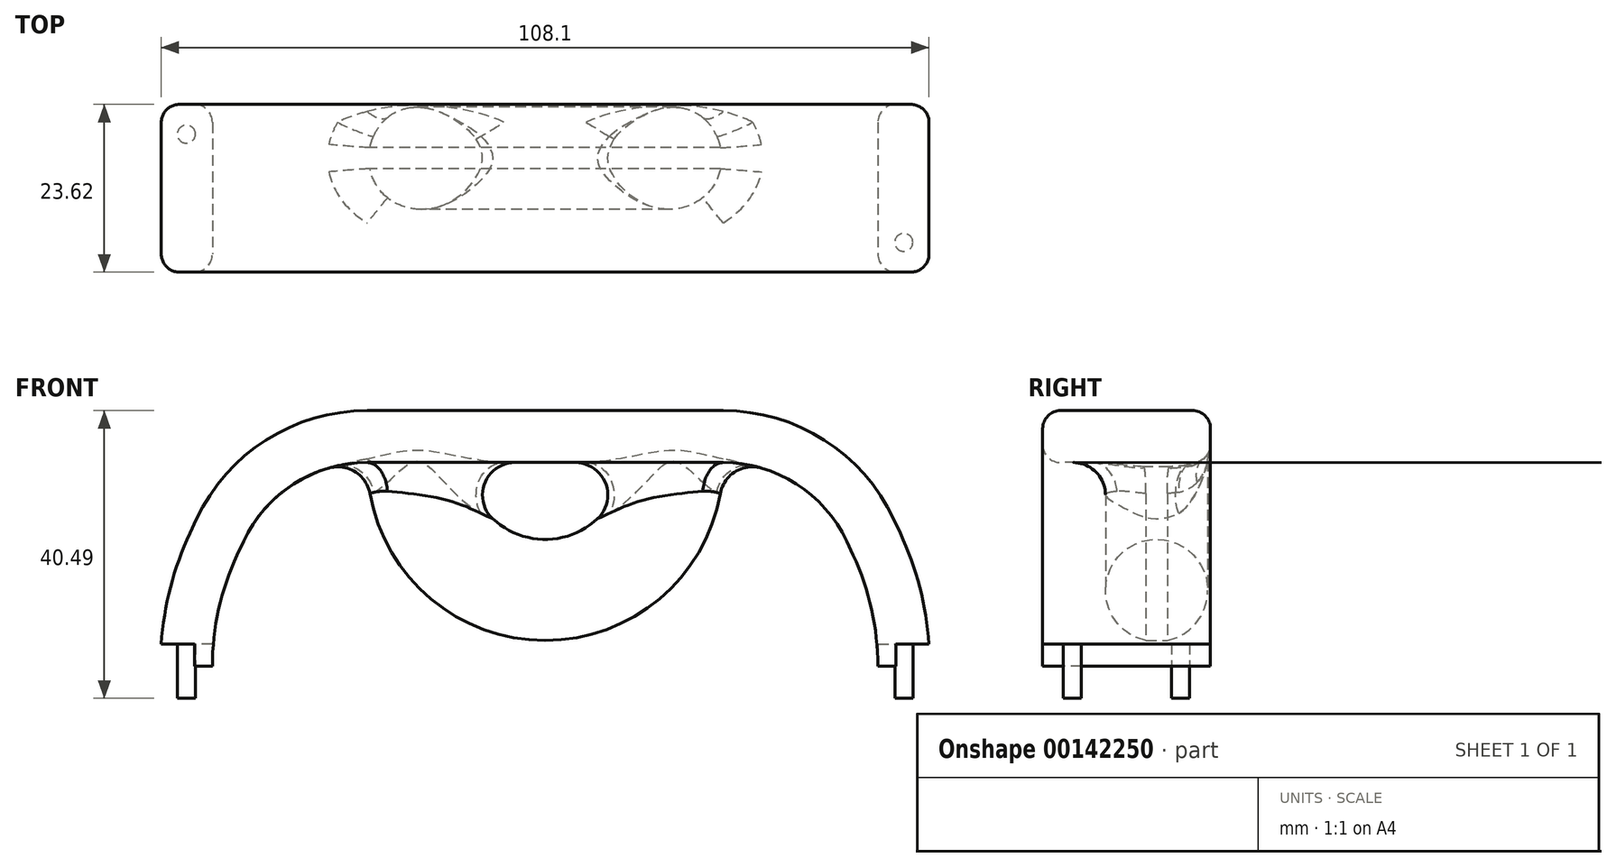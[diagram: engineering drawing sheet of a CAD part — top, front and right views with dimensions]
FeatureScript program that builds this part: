
annotation { "Feature Type Name" : "Feature", "Feature Type Description" : "" }
export const myFeature = defineFeature(function(context is Context, id is Id, definition is map)
    precondition{}
    {
        {
            var Q0;
            Q0=qCreatedBy(makeId("Top.planeOp"),FACE);
            var sketch = newSketch(context, id + "F0", { "sketchPlane" : qUnion([Q0])});
            skLineSegment(sketch, "E0.bottom", {"start": v(49.38, 11.8) * mm, "end": v(51.62, 11.8) * mm});
            skLineSegment(sketch, "E0.top", {"start": v(49.38, -11.8) * mm, "end": v(51.62, -11.8) * mm});
            skLineSegment(sketch, "E0.left", {"start": v(54.16, 9.27) * mm, "end": v(54.16, -9.27) * mm});
            skLineSegment(sketch, "E0.right", {"start": v(46.84, 9.27) * mm, "end": v(46.84, -9.27) * mm});
            skLineSegment(sketch, "E1", {"start": v(0, 14.57) * mm, "end": v(0, -26.63) * mm, "construction": true});
            skCircle(sketch, "E2", {"center": v(50.5, 7.62) * mm, "radius": 1.27 * mm});
            skLineSegment(sketch, "E3", {"start": v(50.5, 11.8) * mm, "end": v(50.5, -11.8) * mm, "construction": true});
            skLineSegment(sketch, "E4", {"start": v(46.84, 0) * mm, "end": v(54.16, 0) * mm, "construction": true});
            skCircle(sketch, "E5.MirrorC", {"center": v(50.5, -7.62) * mm, "radius": 1.27 * mm});
            skLineSegment(sketch, "E6", {"start": v(-32.84, 0) * mm, "end": v(42.72, 0) * mm, "construction": true});
            skCircle(sketch, "E7.MirrorC", {"center": v(-50.5, 7.62) * mm, "radius": 1.27 * mm});
            skCircle(sketch, "E8.MirrorC", {"center": v(-50.5, -7.62) * mm, "radius": 1.27 * mm});
            skPoint(sketch, "E9.visualSharp", {"position": v(46.84, 11.8) * mm});
            skArc(sketch, "E9.filletArc", {"start": v(49.38, 11.8) * mm, "mid": v(47.59, 11.06) * mm, "end": v(46.84, 9.27) * mm});
            skPoint(sketch, "E10.visualSharp", {"position": v(54.16, 11.8) * mm});
            skArc(sketch, "E10.filletArc", {"start": v(54.16, 9.27) * mm, "mid": v(53.41, 11.06) * mm, "end": v(51.62, 11.8) * mm});
            skPoint(sketch, "E11.visualSharp", {"position": v(46.84, -11.8) * mm});
            skArc(sketch, "E11.filletArc", {"start": v(46.84, -9.27) * mm, "mid": v(47.59, -11.06) * mm, "end": v(49.38, -11.8) * mm});
            skPoint(sketch, "E12.visualSharp", {"position": v(54.16, -11.8) * mm});
            skArc(sketch, "E12.filletArc", {"start": v(51.62, -11.8) * mm, "mid": v(53.41, -11.06) * mm, "end": v(54.16, -9.27) * mm});
            skLineSegment(sketch, "E13.MirrorCS", {"start": v(-46.84, 9.27) * mm, "end": v(-46.84, -9.27) * mm});
            skArc(sketch, "E14.MirrorCS", {"start": v(-49.38, 11.8) * mm, "mid": v(-47.59, 11.06) * mm, "end": v(-46.84, 9.27) * mm});
            skLineSegment(sketch, "E15.MirrorCS", {"start": v(-49.38, 11.8) * mm, "end": v(-51.62, 11.8) * mm});
            skArc(sketch, "E16.MirrorCS", {"start": v(-54.16, 9.27) * mm, "mid": v(-53.41, 11.06) * mm, "end": v(-51.62, 11.8) * mm});
            skLineSegment(sketch, "E17.MirrorCS", {"start": v(-54.16, 9.27) * mm, "end": v(-54.16, -9.27) * mm});
            skArc(sketch, "E18.MirrorCS", {"start": v(-51.62, -11.8) * mm, "mid": v(-53.41, -11.06) * mm, "end": v(-54.16, -9.27) * mm});
            skLineSegment(sketch, "E19.MirrorCS", {"start": v(-49.38, -11.8) * mm, "end": v(-51.62, -11.8) * mm});
            skArc(sketch, "E20.MirrorCS", {"start": v(-46.84, -9.27) * mm, "mid": v(-47.59, -11.06) * mm, "end": v(-49.38, -11.8) * mm});
            skSolve(sketch);
        }
        {
            var Q0;
            Q0=qCreatedBy(makeId("Front.planeOp"),FACE);
            var sketch = newSketch(context, id + "F1", { "sketchPlane" : qUnion([Q0])});
            skPoint(sketch, "E21.0", {"position": v(-50.5, 0) * mm});
            skPoint(sketch, "E22.0", {"position": v(50.5, 0) * mm});
            skLineSegment(sketch, "E23", {"start": v(-50.5, 0) * mm, "end": v(-50.5, 4.48) * mm});
            skLineSegment(sketch, "E24", {"start": v(-46.68, 21.68) * mm, "end": v(-45.76, 23.64) * mm});
            skLineSegment(sketch, "E25", {"start": v(-25.05, 36.83) * mm, "end": v(0, 36.83) * mm});
            skLineSegment(sketch, "E26", {"start": v(0, 38.28) * mm, "end": v(0, -45.27) * mm, "construction": true});
            skPoint(sketch, "E27.visualSharp", {"position": v(-39.6, 36.83) * mm});
            skArc(sketch, "E27.filletArc", {"start": v(-25.05, 36.83) * mm, "mid": v(-37.33, 33.25) * mm, "end": v(-45.76, 23.64) * mm});
            skPoint(sketch, "E28.visualSharp", {"position": v(-50.5, 13.5) * mm});
            skArc(sketch, "E28.filletArc", {"start": v(-46.68, 21.68) * mm, "mid": v(-49.53, 13.29) * mm, "end": v(-50.5, 4.48) * mm});
            skLineSegment(sketch, "E29.MirrorCS", {"start": v(25.05, 36.83) * mm, "end": v(0, 36.83) * mm});
            skArc(sketch, "E30.MirrorCS", {"start": v(25.05, 36.83) * mm, "mid": v(37.33, 33.25) * mm, "end": v(45.76, 23.64) * mm});
            skLineSegment(sketch, "E31.MirrorCS", {"start": v(46.68, 21.68) * mm, "end": v(45.76, 23.64) * mm});
            skArc(sketch, "E32.MirrorCS", {"start": v(46.68, 21.68) * mm, "mid": v(49.53, 13.29) * mm, "end": v(50.5, 4.48) * mm});
            skLineSegment(sketch, "E33.MirrorCS", {"start": v(50.5, 0) * mm, "end": v(50.5, 4.48) * mm});
            skSolve(sketch);
        }
        {
            var Q0;
            Q0=makeQuery(id+"F0.imprint","IMPRINT",FACE,{"disambiguationData":[TD([[makeQuery(id+"F0.imprint","IMPRINT",EDGE,{"derivedFrom":sQuery(id+"F0.wireOp",EDGE,"E7.MirrorC")}),1.0]])]});
            var Q1;
            Q1=makeQuery(id+"F0.imprint","IMPRINT",FACE,{"disambiguationData":[TD([[makeQuery(id+"F0.imprint","IMPRINT",EDGE,{"derivedFrom":sQuery(id+"F0.wireOp",EDGE,"E8.MirrorC")}),1.0]])]});
            var Q2;
            Q2=makeQuery(id+"F0.imprint","IMPRINT",FACE,{"disambiguationData":[TD([[makeQuery(id+"F0.imprint","IMPRINT",EDGE,{"derivedFrom":sQuery(id+"F0.wireOp",EDGE,"E7.MirrorC")}),-1.0]])]});
            var Q3;
            Q3=sQuery(id+"F1.wireOp",EDGE,"E23");
            var Q4;
            Q4=sQuery(id+"F1.wireOp",EDGE,"E28.filletArc");
            var Q5;
            Q5=sQuery(id+"F1.wireOp",EDGE,"E24");
            var Q6;
            Q6=sQuery(id+"F1.wireOp",EDGE,"E27.filletArc");
            var Q7;
            Q7=sQuery(id+"F1.wireOp",EDGE,"E25");
            var Q8;
            Q8=sQuery(id+"F1.wireOp",EDGE,"E29.MirrorCS");
            var Q9;
            Q9=sQuery(id+"F1.wireOp",EDGE,"E30.MirrorCS");
            var Q10;
            Q10=sQuery(id+"F1.wireOp",EDGE,"E31.MirrorCS");
            var Q11;
            Q11=sQuery(id+"F1.wireOp",EDGE,"E32.MirrorCS");
            var Q12;
            Q12=sQuery(id+"F1.wireOp",EDGE,"E33.MirrorCS");
            sweep(context, id + "F2", {"profiles" : qUnion([Q0, Q1, Q2]), "path" : qUnion([Q3, Q4, Q5, Q6, Q7, Q8, Q9, Q10, Q11, Q12])});
        }
        {
            var Q0;
            Q0=makeQuery(id+"F2.opSweep","SWEPT_FACE",FACE,{"disambiguationData":[OSD([sQuery(id+"F0.wireOp",EDGE,"E13.MirrorCS"),sQuery(id+"F1.wireOp",EDGE,"E25")])]});
            var sketch = newSketch(context, id + "F3", { "sketchPlane" : qUnion([Q0])});
            skLineSegment(sketch, "E34", {"start": v(0, -17.35) * mm, "end": v(0, 18.28) * mm, "construction": true});
            skPoint(sketch, "E34.endSnap0", {"position": v(0, 9.27) * mm});
            skLineSegment(sketch, "E35.0", {"start": v(-25.05, -11.8) * mm, "end": v(25.05, -11.8) * mm, "construction": true});
            skLineSegment(sketch, "E36.0", {"start": v(-25.05, 11.8) * mm, "end": v(25.05, 11.8) * mm, "construction": true});
            skCircle(sketch, "E37", {"center": v(18.01, -4.23) * mm, "radius": 7.2 * mm});
            skSolve(sketch);
        }
        {
            var Q0;
            {var subQ0=sQuery(id+"F3.wireOp",EDGE,"E37");var subQ1=makeQuery(id+"F2.opSweep","SWEPT_EDGE",EDGE,{"disambiguationData":[OSD([sQuery(id+"F0.wireOp",EDGE,"E13.MirrorCS"),sQuery(id+"F0.wireOp",EDGE,"E14.MirrorCS"),sQuery(id+"F1.wireOp",EDGE,"E25")])]});var subQ2=makeQuery(id+"F3.imprint","INTERSECT",VERTEX,{"disambiguationData":[OD(0.0)],"derivedFrom":[subQ1,subQ0]});Q0=makeQuery(id+"F3.imprint","IMPRINT",FACE,{"disambiguationData":[TD([[makeQuery(id+"F3.imprint","IMPRINT",EDGE,{"disambiguationData":[TD([[subQ2,-1.0]])],"derivedFrom":subQ0}),1.0]])]});}
            var Q1;
            {var subQ0=sQuery(id+"F3.wireOp",EDGE,"E37");var subQ1=makeQuery(id+"F2.opSweep","SWEPT_EDGE",EDGE,{"disambiguationData":[OSD([sQuery(id+"F0.wireOp",EDGE,"E13.MirrorCS"),sQuery(id+"F0.wireOp",EDGE,"E14.MirrorCS"),sQuery(id+"F1.wireOp",EDGE,"E25")])]});var subQ2=makeQuery(id+"F3.imprint","INTERSECT",VERTEX,{"disambiguationData":[OD(0.0)],"derivedFrom":[subQ1,subQ0]});Q1=makeQuery(id+"F3.imprint","IMPRINT",FACE,{"disambiguationData":[TD([[makeQuery(id+"F3.imprint","IMPRINT",EDGE,{"disambiguationData":[TD([[subQ2,1.0]])],"derivedFrom":subQ0}),1.0]])]});}
            var Q2;
            Q2=sQuery(id+"F3.wireOp",EDGE,"E34");
            revolve(context, id + "F4", {"operationType" : NewBodyOperationType.ADD, "entities" : qUnion([Q0, Q1]), "axis" : qUnion([Q2]), "revolveType" : RevolveType.TWO_DIRECTIONS, "angle" : 15.1 * degree, "angleBack" : 164.53 * degree});
        }
        {
            var Q0;
            Q0=makeQuery(id+"F4.boolean.opBoolean","INTERSECT",EDGE,{"disambiguationData":[OD(1.0)],"derivedFrom":[makeQuery(id+"F2.opSweep","SWEPT_FACE",FACE,{"disambiguationData":[OSD([sQuery(id+"F0.wireOp",EDGE,"E13.MirrorCS"),sQuery(id+"F1.wireOp",EDGE,"E25")])]}),makeQuery(id+"F4.opRevolve","SWEPT_FACE",FACE,{"disambiguationData":[OSD([sQuery(id+"F3.wireOp",EDGE,"E37")])]})]});
            var Q1;
            {var subQ0=sQuery(id+"F0.wireOp",EDGE,"E13.MirrorCS");var subQ1=sQuery(id+"F1.wireOp",VERTEX,"E30.MirrorCS.start");Q1=makeQuery(id+"F4.boolean.opBoolean","SPLIT",EDGE,{"disambiguationData":[topologyDisambiguationEdgeConnected([makeQuery(id+"F2.opSweep","SWEPT_FACE",FACE,{"disambiguationData":[OSD([subQ0,sQuery(id+"F1.wireOp",EDGE,"E30.MirrorCS")])]}),makeQuery(id+"F4.opRevolve","SWEPT_FACE",FACE,{"disambiguationData":[OSD([subQ0,subQ1])]})])],"derivedFrom":makeQuery(id+"F2.opSweep","MID_CAP_EDGE",EDGE,{"disambiguationData":[OSD([subQ0,subQ1])],"capPos":6.0})});}
            var Q2;
            Q2=makeQuery(id+"F4.boolean.opBoolean","INTERSECT",EDGE,{"disambiguationData":[OD(0.0)],"derivedFrom":[makeQuery(id+"F2.opSweep","SWEPT_FACE",FACE,{"disambiguationData":[OSD([sQuery(id+"F0.wireOp",EDGE,"E14.MirrorCS"),sQuery(id+"F1.wireOp",EDGE,"E25")])]}),makeQuery(id+"F4.opRevolve","SWEPT_FACE",FACE,{"disambiguationData":[OSD([sQuery(id+"F3.wireOp",EDGE,"E37")])]})]});
            var Q3;
            Q3=makeQuery(id+"F4.boolean.opBoolean","INTERSECT",EDGE,{"disambiguationData":[OD(2.0)],"derivedFrom":[makeQuery(id+"F2.opSweep","SWEPT_FACE",FACE,{"disambiguationData":[OSD([sQuery(id+"F0.wireOp",EDGE,"E13.MirrorCS"),sQuery(id+"F1.wireOp",EDGE,"E25")])]}),makeQuery(id+"F4.opRevolve","SWEPT_FACE",FACE,{"disambiguationData":[OSD([sQuery(id+"F3.wireOp",EDGE,"E37")])]})]});
            var Q4;
            {var subQ0=sQuery(id+"F0.wireOp",EDGE,"E13.MirrorCS");Q4=makeQuery(id+"F4.boolean.opBoolean","SPLIT",EDGE,{"disambiguationData":[topologyDisambiguationEdgeConnected([makeQuery(id+"F2.opSweep","SWEPT_FACE",FACE,{"disambiguationData":[OSD([subQ0,sQuery(id+"F1.wireOp",EDGE,"E27.filletArc")])]}),makeQuery(id+"F4.opRevolve","SWEPT_FACE",FACE,{"disambiguationData":[OSD([subQ0,sQuery(id+"F1.wireOp",VERTEX,"E30.MirrorCS.start")])]})])],"derivedFrom":makeQuery(id+"F2.opSweep","MID_CAP_EDGE",EDGE,{"disambiguationData":[OSD([subQ0,sQuery(id+"F1.wireOp",VERTEX,"E25.start")])],"capPos":4.0})});}
            fillet(context, id + "F5", {"entities" : qUnion([Q0, Q1, Q2, Q3, Q4]), "radius" : 4.57 * mm, "tangentPropagation" : true, "allowEdgeOverflow" : false});
        }
        {
            var Q0;
            Q0=makeQuery(id+"F0.imprint","IMPRINT",FACE,{"disambiguationData":[TD([[makeQuery(id+"F0.imprint","IMPRINT",EDGE,{"derivedFrom":sQuery(id+"F0.wireOp",EDGE,"E2")}),1.0]])]});
            var Q1;
            Q1=makeQuery(id+"F0.imprint","IMPRINT",FACE,{"disambiguationData":[TD([[makeQuery(id+"F0.imprint","IMPRINT",EDGE,{"derivedFrom":sQuery(id+"F0.wireOp",EDGE,"E5.MirrorC")}),-1.0]])]});
            var Q2;
            Q2=makeQuery(id+"F0.imprint","IMPRINT",FACE,{"disambiguationData":[TD([[makeQuery(id+"F0.imprint","IMPRINT",EDGE,{"derivedFrom":sQuery(id+"F0.wireOp",EDGE,"E7.MirrorC")}),-1.0]])]});
            var Q3;
            Q3=makeQuery(id+"F0.imprint","IMPRINT",FACE,{"disambiguationData":[TD([[makeQuery(id+"F0.imprint","IMPRINT",EDGE,{"derivedFrom":sQuery(id+"F0.wireOp",EDGE,"E8.MirrorC")}),1.0]])]});
            extrude(context, id + "F6", {"entities" : qUnion([Q0, Q1, Q2, Q3]), "operationType" : NewBodyOperationType.REMOVE, "depth" : 7.62 * mm});
        }
    });
